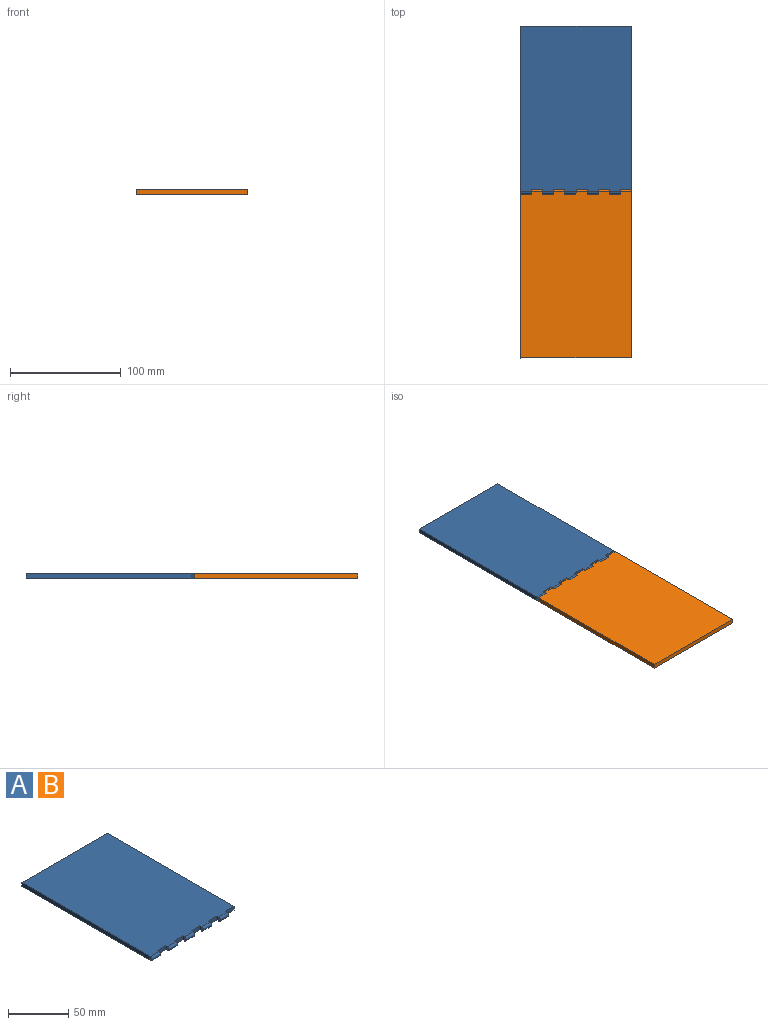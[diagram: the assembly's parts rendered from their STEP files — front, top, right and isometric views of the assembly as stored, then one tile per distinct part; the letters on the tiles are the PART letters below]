
ASSEMBLY  parts=2 mates=1
PART A: 29 faces, bbox 100x152x4 mm
  f0: plane 150x100mm, normal (0,0,1), area 14895mm2, adj f2,f3,f4,f5,f6,f7,f8,f9
  f1: plane 150x100mm, normal (0,0,-1), area 14895mm2, adj f2,f3,f4,f5,f6,f7,f8,f9
  f2: cylinder r=2mm len=10mm, axis (1,0,0), area 62.8mm2, adj f0,f1,f21,f23
  f3: cylinder r=2mm len=10mm, axis (1,0,0), area 62.8mm2, adj f0,f1,f18,f20
  f4: cylinder r=2mm len=10mm, axis (1,0,0), area 62.8mm2, adj f0,f1,f15,f17
  f5: cylinder r=2mm len=10mm, axis (1,0,0), area 62.8mm2, adj f0,f1,f12,f14
  f6: cylinder r=2mm len=10mm, axis (1,0,0), area 62.8mm2, adj f0,f1,f7,f11
  f7: plane 152x4mm, normal (-1,0,0), area 605.4mm2, adj f0,f1,f6,f9,f28
  f8: plane 147.9x4mm, normal (1,0,0), area 591.6mm2, adj f0,f1,f9,f22
  f9: plane 100x4mm, normal (0,1,0), area 400mm2, adj f0,f1,f7,f8
  f10: plane 10x4mm, normal (0,-1,0), area 40mm2, adj f0,f1,f11,f12
  f11: plane 4.1x4mm, normal (1,0,0), area 13.8mm2, adj f0,f1,f6,f10,f28
  f12: plane 4.1x4mm, normal (-1,0,0), area 13.8mm2, adj f0,f1,f5,f10,f27
  f13: plane 10x4mm, normal (0,-1,0), area 40mm2, adj f0,f1,f14,f15
  f14: plane 4.1x4mm, normal (1,0,0), area 13.8mm2, adj f0,f1,f5,f13,f27
  f15: plane 4.1x4mm, normal (-1,0,0), area 13.8mm2, adj f0,f1,f4,f13,f26
  f16: plane 10x4mm, normal (0,-1,0), area 40mm2, adj f0,f1,f17,f18
  f17: plane 4.1x4mm, normal (1,0,0), area 13.8mm2, adj f0,f1,f4,f16,f26
  f18: plane 4.1x4mm, normal (-1,0,0), area 13.8mm2, adj f0,f1,f3,f16,f25
  f19: plane 10x4mm, normal (0,-1,0), area 40mm2, adj f0,f1,f20,f21
  f20: plane 4.1x4mm, normal (1,0,0), area 13.8mm2, adj f0,f1,f3,f19,f25
  f21: plane 4.1x4mm, normal (-1,0,0), area 13.8mm2, adj f0,f1,f2,f19,f24
  f22: plane 10x4mm, normal (0,-1,0), area 40mm2, adj f0,f1,f8,f23
  f23: plane 4.1x4mm, normal (1,0,0), area 13.8mm2, adj f0,f1,f2,f22,f24
  f24: cylinder r=0.52mm len=10mm, axis (-1,0,0), area 32.8mm2, adj f21,f23
  f25: cylinder r=0.52mm len=10mm, axis (-1,0,0), area 32.8mm2, adj f18,f20
  f26: cylinder r=0.52mm len=10mm, axis (-1,0,0), area 32.8mm2, adj f15,f17
  f27: cylinder r=0.52mm len=10mm, axis (-1,0,0), area 32.8mm2, adj f12,f14
  f28: cylinder r=0.52mm len=10mm, axis (-1,0,0), area 32.8mm2, adj f7,f11
PART B: same geometry as A
PLACE A t=(96.74,-6.67,-0.32)mm
PLACE B rot(axis=(0,0,-1),180deg) t=(185.07,-99.67,-0.32)mm
MATE revolute A.f2 <-> B.f2  axis (-1,0,0) through (90.91,-53.17,1.68)mm
